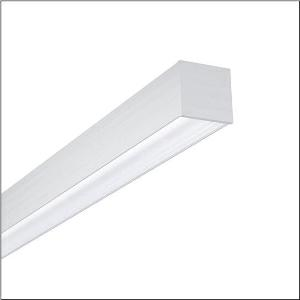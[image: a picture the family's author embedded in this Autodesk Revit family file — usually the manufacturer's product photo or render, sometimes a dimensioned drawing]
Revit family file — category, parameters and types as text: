
# Revit family: silica_r_5mx22wd1e4a_75c3
name_source: partatom
category: Lighting Fixtures
units: mm (PartAtom-declared; Revit-internal decimal feet)

## family parameters
Cut with Voids When Loaded = No
Host = Face
Light Source = No
Part Type = Normal
Room Calculation Point = No
Round Connector Dimension = Use Diameter
Shared = No

## types (1)
- --- (1 x LED, 4680 lm, 29.3 W, 4000K)
    Apparent Load = 29 VA
    CIE Flux Codes = 70 95 99 100 100
    Color Rendering = 80
    Color Temperature = 4000K
    Default Elevation = 1800 mm
    Description = Silica®, office luminaire, primary light control with wallwasher, of aluminium, light emission: direct distribution, primary light characteristic: asymmetric, installation type: surface-mounted, LED, rated luminous flux: 4.680lm, luminous efficacy: 160lm/W, light colour: 840, colour temperature: 4000K, control gear: ECG DALI, with terminal, 3+2-pole, max. 2.5mm², mains connection: 230V, AC, 50/60Hz, rated input power: 29W, luminaire housing, of aluminium, anodised, silver, length: 1.442mm, width: 65mm, height: 64mm, protection rating (complete): IP20, insulation class (complete): insulation class I (protective earthing), certification: CE, permissible operating ambient temperature: 0..+35°C, standard: EN 50419, packaging unit: 1 piece
    Height = 64 mm
    Lamp = 1 x LED
    Lamp Light Flux = 4680 lm
    Lamp Power = 29.3 W
    Lamp count = 1
    Length = 1442 mm
    Luminous efficacy = 160 lm/W
    Manufacturer = Siteco
    ModVariant = No
    Model = 5MX22WD1E4A
    Mounting Place = Ceiling
    Mounting Type = Surface mounted
    Number of Poles = 1
    OnlyDefault = Yes
    Power Factor = 1
    Product Name = Silica®
    Product group = office luminaire | ceiling mounted
    ProductGroupID = 300
    Protection Class = Protection class I
    Protection Degree = IP 20
    RLX_Detail_Level = 1
    RLX_Emergency_Light_Flux = 0 lm
    RLX_Emergency_Type = 0
    RLX_Emergency_Type_DB = No
    RlxData = <blob elided: 27893 chars, md5=0507e680>
    Socket = socket
    Standby Power = 0 W
    System Light Flux = 4680 lm
    System Power = 29 W
    Type Comments = factory setting: luminous flux: 100 % | dim-lin: 254 | 164 mA
    Type Image = l_1004827.jpg
    URL = http://relux.com
    VarID = @adj_155046
    Voltage = 0 V
    Weight = 0.00 kg
    Width = 66 mm

## geometry (parser evidence)
native form markers: Blend x4, Sweep x12
no freeform markers — native parametric forms only
